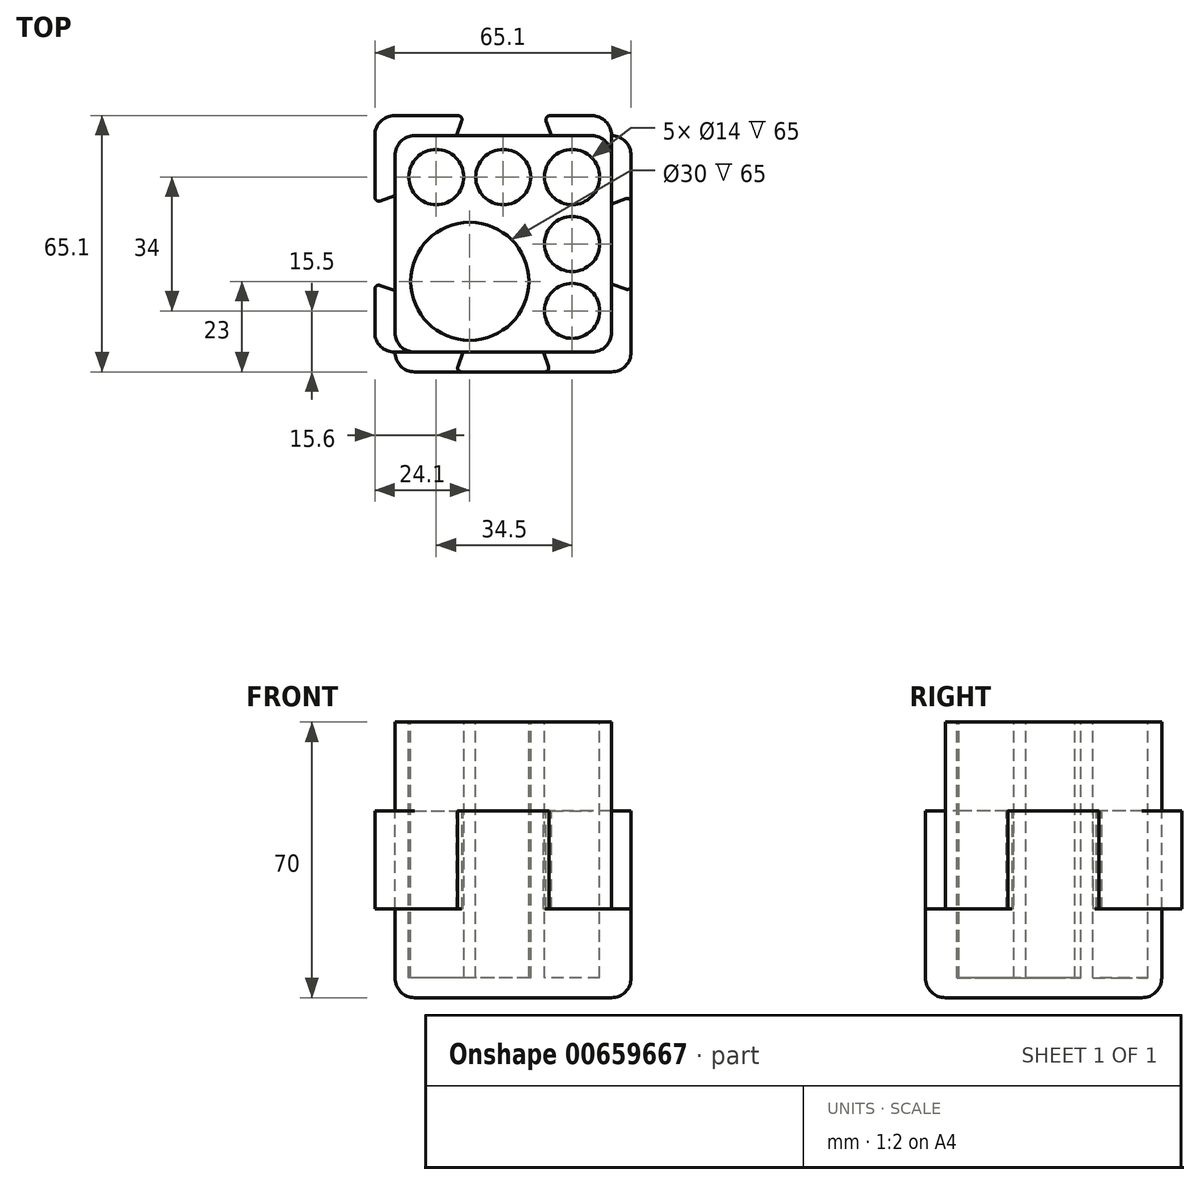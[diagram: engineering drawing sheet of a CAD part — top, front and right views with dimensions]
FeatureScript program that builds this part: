
annotation { "Feature Type Name" : "Feature", "Feature Type Description" : "" }
export const myFeature = defineFeature(function(context is Context, id is Id, definition is map)
    precondition{}
    {
        {
            var Q0;
            Q0=qCreatedBy(makeId("Top.planeOp"),FACE);
            var sketch = newSketch(context, id + "F0", { "sketchPlane" : qUnion([Q0])});
            skLineSegment(sketch, "E0.bottom", {"start": v(-27.5, 27.5) * mm, "end": v(27.5, 27.5) * mm});
            skLineSegment(sketch, "E0.top", {"start": v(-27.5, -27.5) * mm, "end": v(27.5, -27.5) * mm});
            skLineSegment(sketch, "E0.left", {"start": v(-27.5, 27.5) * mm, "end": v(-27.5, -27.5) * mm});
            skLineSegment(sketch, "E0.right", {"start": v(27.5, 27.5) * mm, "end": v(27.5, -27.5) * mm});
            skPoint(sketch, "E0.middle", {"position": v(0, 0) * mm});
            skLineSegment(sketch, "E1", {"start": v(-27.5, 27.5) * mm, "end": v(-32.6, 27.5) * mm});
            skLineSegment(sketch, "E2", {"start": v(-32.6, 27.5) * mm, "end": v(-32.6, 10.44) * mm});
            skLineSegment(sketch, "E3", {"start": v(-32.6, 10.44) * mm, "end": v(-27.5, 12.3) * mm});
            skLineSegment(sketch, "E4", {"start": v(-27.5, -11.9) * mm, "end": v(-32.6, -10.04) * mm});
            skLineSegment(sketch, "E5", {"start": v(-32.6, -10.04) * mm, "end": v(-32.6, -27.5) * mm});
            skLineSegment(sketch, "E6", {"start": v(-32.6, -27.5) * mm, "end": v(-27.5, -27.5) * mm});
            skLineSegment(sketch, "E7", {"start": v(-27.5, 27.5) * mm, "end": v(-27.5, 32.6) * mm});
            skLineSegment(sketch, "E8", {"start": v(-27.5, 32.6) * mm, "end": v(-10.04, 32.6) * mm});
            skLineSegment(sketch, "E9", {"start": v(-10.04, 32.6) * mm, "end": v(-11.9, 27.5) * mm});
            skLineSegment(sketch, "E10", {"start": v(27.5, 27.5) * mm, "end": v(27.5, 32.6) * mm});
            skLineSegment(sketch, "E11", {"start": v(27.5, 32.6) * mm, "end": v(10.44, 32.6) * mm});
            skLineSegment(sketch, "E12", {"start": v(10.44, 32.6) * mm, "end": v(12.3, 27.5) * mm});
            skLineSegment(sketch, "E13", {"start": v(-10.18, -27.5) * mm, "end": v(-12, -32.5) * mm});
            skLineSegment(sketch, "E14", {"start": v(-12, -32.5) * mm, "end": v(12, -32.5) * mm});
            skLineSegment(sketch, "E15", {"start": v(12, -32.5) * mm, "end": v(10.18, -27.5) * mm});
            skPoint(sketch, "E16", {"position": v(0, -32.5) * mm});
            skLineSegment(sketch, "E17", {"start": v(27.5, -10.18) * mm, "end": v(32.5, -12) * mm});
            skLineSegment(sketch, "E18", {"start": v(32.5, -12) * mm, "end": v(32.5, 12) * mm});
            skLineSegment(sketch, "E19", {"start": v(32.5, 12) * mm, "end": v(27.5, 10.18) * mm});
            skPoint(sketch, "E20", {"position": v(32.5, 0) * mm});
            skLineSegment(sketch, "E21", {"start": v(-32.6, 27.5) * mm, "end": v(-32.6, 32.6) * mm});
            skLineSegment(sketch, "E22", {"start": v(-32.6, 32.6) * mm, "end": v(-27.5, 32.6) * mm});
            skSolve(sketch);
        }
        {
            var Q0;
            {var subQ1=sQuery(id+"F0.wireOp",EDGE,"E0.bottom");Q0=makeQuery(id+"F0.imprint","IMPRINT",FACE,{"disambiguationData":[TD([[makeQuery(id+"F0.imprint","IMPRINT",EDGE,{"derivedFrom":subQ1}),-1.0]])]});}
            extrude(context, id + "F1", {"entities" : qUnion([Q0]), "oppositeDirection" : true, "depth" : 70 * mm, "offsetDistance" : 25 * mm, "symmetric" : true});
        }
        {
            var Q0;
            {var subQ0=sQuery(id+"F0.wireOp",EDGE,"E1");Q0=makeQuery(id+"F0.imprint","IMPRINT",FACE,{"disambiguationData":[TD([[makeQuery(id+"F0.imprint","IMPRINT",EDGE,{"derivedFrom":subQ0}),1.0]])]});}
            var Q1;
            {var subQ2=sQuery(id+"F0.wireOp",EDGE,"E4");Q1=makeQuery(id+"F0.imprint","IMPRINT",FACE,{"disambiguationData":[TD([[makeQuery(id+"F0.imprint","IMPRINT",EDGE,{"derivedFrom":subQ2}),1.0]])]});}
            var Q2;
            {var subQ2=sQuery(id+"F0.wireOp",EDGE,"E7");Q2=makeQuery(id+"F0.imprint","IMPRINT",FACE,{"disambiguationData":[TD([[makeQuery(id+"F0.imprint","IMPRINT",EDGE,{"derivedFrom":subQ2}),-1.0]])]});}
            var Q3;
            {var subQ0=sQuery(id+"F0.wireOp",EDGE,"E10");Q3=makeQuery(id+"F0.imprint","IMPRINT",FACE,{"disambiguationData":[TD([[makeQuery(id+"F0.imprint","IMPRINT",EDGE,{"derivedFrom":subQ0}),1.0]])]});}
            var Q4;
            {var subQ2=sQuery(id+"F0.wireOp",EDGE,"E13");Q4=makeQuery(id+"F0.imprint","IMPRINT",FACE,{"disambiguationData":[TD([[makeQuery(id+"F0.imprint","IMPRINT",EDGE,{"derivedFrom":subQ2}),1.0]])]});}
            var Q5;
            {var subQ0=sQuery(id+"F0.wireOp",EDGE,"E17");Q5=makeQuery(id+"F0.imprint","IMPRINT",FACE,{"disambiguationData":[TD([[makeQuery(id+"F0.imprint","IMPRINT",EDGE,{"derivedFrom":subQ0}),1.0]])]});}
            var Q6;
            Q6=makeQuery(id+"F0.imprint","IMPRINT",FACE,{"disambiguationData":[TD([[makeQuery(id+"F0.imprint","IMPRINT",EDGE,{"derivedFrom":sQuery(id+"F0.wireOp",EDGE,"E1")}),-1.0]])]});
            extrude(context, id + "F2", {"entities" : qUnion([Q0, Q1, Q2, Q3, Q4, Q5, Q6]), "operationType" : NewBodyOperationType.ADD, "oppositeDirection" : true, "depth" : 25 * mm, "offsetDistance" : 25 * mm, "symmetric" : true});
        }
        {
            var Q0;
            Q0=makeQuery(id+"F1.opExtrude","CAP_FACE",FACE,{"disambiguationData":[OSD([sQuery(id+"F0.wireOp",EDGE,"E0.bottom"),sQuery(id+"F0.wireOp",EDGE,"E0.top"),sQuery(id+"F0.wireOp",EDGE,"E0.left"),sQuery(id+"F0.wireOp",EDGE,"E0.right")])],"isStart":false});
            var sketch = newSketch(context, id + "F3", { "sketchPlane" : qUnion([Q0])});
            skLineSegment(sketch, "E23", {"start": v(-27.5, 27.5) * mm, "end": v(-27.5, 32.5) * mm});
            skLineSegment(sketch, "E24", {"start": v(-27.5, 32.5) * mm, "end": v(32.5, 32.5) * mm});
            skLineSegment(sketch, "E25", {"start": v(32.5, 32.5) * mm, "end": v(32.5, -27.5) * mm});
            skLineSegment(sketch, "E26", {"start": v(32.5, -27.5) * mm, "end": v(27.5, -27.5) * mm});
            skLineSegment(sketch, "E27", {"start": v(27.5, -27.5) * mm, "end": v(27.5, 27.5) * mm});
            skLineSegment(sketch, "E28", {"start": v(27.5, 27.5) * mm, "end": v(-27.5, 27.5) * mm});
            skSolve(sketch);
        }
        {
            var Q0;
            Q0 = qSketchRegion(id + "F3", true);
            var Q1;
            Q1=makeQuery(id+"F2.opExtrude","CAP_FACE",FACE,{"disambiguationData":[OSD([sQuery(id+"F0.wireOp",EDGE,"E0.right"),sQuery(id+"F0.wireOp",EDGE,"E17"),sQuery(id+"F0.wireOp",EDGE,"E18"),sQuery(id+"F0.wireOp",EDGE,"E19")])],"isStart":false});
            extrude(context, id + "F4", {"entities" : qUnion([Q0]), "operationType" : NewBodyOperationType.ADD, "endBound" : BoundingType.UP_TO_SURFACE, "oppositeDirection" : true, "depth" : 25 * mm, "endBoundEntityFace" : qUnion([Q1]), "offsetDistance" : 25 * mm});
        }
        {
            var Q0;
            Q0=makeQuery(id+"F2.opExtrude","SWEPT_EDGE",EDGE,{"disambiguationData":[OSD([sQuery(id+"F0.wireOp",EDGE,"E21"),sQuery(id+"F0.wireOp",EDGE,"E22")])]});
            var Q1;
            {var subQ0=sQuery(id+"F0.wireOp",EDGE,"E0.bottom");var subQ1=sQuery(id+"F0.wireOp",EDGE,"E0.left");Q1=makeQuery(id+"F2.boolean.opBoolean","SPLIT",EDGE,{"disambiguationData":[TD([makeQuery(id+"F1.opExtrude","CAP_FACE",FACE,{"disambiguationData":[OSD([subQ0,sQuery(id+"F0.wireOp",EDGE,"E0.top"),subQ1,sQuery(id+"F0.wireOp",EDGE,"E0.right")])],"isStart":true})])],"derivedFrom":makeQuery(id+"F1.opExtrude","SWEPT_EDGE",EDGE,{"disambiguationData":[OSD([subQ0,subQ1,sQuery(id+"F0.wireOp",EDGE,"E1"),sQuery(id+"F0.wireOp",EDGE,"E7")])]})});}
            var Q2;
            {var subQ0=sQuery(id+"F0.wireOp",EDGE,"E0.bottom");var subQ1=sQuery(id+"F0.wireOp",EDGE,"E0.left");Q2=makeQuery(id+"F2.boolean.opBoolean","SPLIT",EDGE,{"disambiguationData":[TD([makeQuery(id+"F1.opExtrude","CAP_FACE",FACE,{"disambiguationData":[OSD([subQ0,sQuery(id+"F0.wireOp",EDGE,"E0.top"),subQ1,sQuery(id+"F0.wireOp",EDGE,"E0.right")])],"isStart":false})])],"derivedFrom":makeQuery(id+"F1.opExtrude","SWEPT_EDGE",EDGE,{"disambiguationData":[OSD([subQ0,subQ1,sQuery(id+"F0.wireOp",EDGE,"E1"),sQuery(id+"F0.wireOp",EDGE,"E7")])]})});}
            var Q3;
            Q3=makeQuery(id+"F2.opExtrude","SWEPT_EDGE",EDGE,{"disambiguationData":[OSD([sQuery(id+"F0.wireOp",EDGE,"E5"),sQuery(id+"F0.wireOp",EDGE,"E6")])]});
            var Q4;
            Q4=makeQuery(id+"F4.opExtrude","SWEPT_EDGE",EDGE,{"disambiguationData":[OSD([sQuery(id+"F3.wireOp",EDGE,"E23"),sQuery(id+"F3.wireOp",EDGE,"E24")])]});
            var Q5;
            Q5=makeQuery(id+"F4.opExtrude","SWEPT_EDGE",EDGE,{"disambiguationData":[OSD([sQuery(id+"F3.wireOp",EDGE,"E24"),sQuery(id+"F3.wireOp",EDGE,"E25")])]});
            var Q6;
            Q6=makeQuery(id+"F1.opExtrude","SWEPT_EDGE",EDGE,{"disambiguationData":[OSD([sQuery(id+"F0.wireOp",EDGE,"E0.top"),sQuery(id+"F0.wireOp",EDGE,"E0.right")])]});
            var Q7;
            Q7=makeQuery(id+"F4.opExtrude","SWEPT_EDGE",EDGE,{"disambiguationData":[OSD([sQuery(id+"F3.wireOp",EDGE,"E25"),sQuery(id+"F3.wireOp",EDGE,"E26")])]});
            var Q8;
            Q8=makeQuery(id+"F2.opExtrude","SWEPT_EDGE",EDGE,{"disambiguationData":[OSD([sQuery(id+"F0.wireOp",EDGE,"E10"),sQuery(id+"F0.wireOp",EDGE,"E11")])]});
            var Q9;
            {var subQ0=sQuery(id+"F0.wireOp",EDGE,"E0.right");var subQ1=sQuery(id+"F0.wireOp",EDGE,"E0.bottom");var subQ2=sQuery(id+"F0.wireOp",EDGE,"E10");Q9=makeQuery(id+"F2.boolean.opBoolean","SPLIT",EDGE,{"disambiguationData":[TD([makeQuery(id+"F1.opExtrude","CAP_FACE",FACE,{"disambiguationData":[OSD([subQ1,sQuery(id+"F0.wireOp",EDGE,"E0.top"),sQuery(id+"F0.wireOp",EDGE,"E0.left"),subQ0])],"isStart":true})])],"derivedFrom":makeQuery(id+"F1.opExtrude","SWEPT_EDGE",EDGE,{"disambiguationData":[OSD([subQ1,subQ0,subQ2])]})});}
            var Q10;
            Q10=makeQuery(id+"F4.opExtrude","CAP_EDGE",EDGE,{"disambiguationData":[OSD([sQuery(id+"F3.wireOp",EDGE,"E25")])],"isStart":true});
            var Q11;
            Q11=makeQuery(id+"F4.opExtrude","CAP_EDGE",EDGE,{"disambiguationData":[OSD([sQuery(id+"F3.wireOp",EDGE,"E24")])],"isStart":true});
            var Q12;
            Q12=makeQuery(id+"F4.boolean.opBoolean","MERGE",EDGE,{"derivedFrom":[makeQuery(id+"F1.opExtrude","CAP_EDGE",EDGE,{"disambiguationData":[OSD([sQuery(id+"F0.wireOp",EDGE,"E0.left")])],"isStart":false}),makeQuery(id+"F4.opExtrude","CAP_EDGE",EDGE,{"disambiguationData":[OSD([sQuery(id+"F3.wireOp",EDGE,"E23")])],"isStart":true})]});
            var Q13;
            Q13=makeQuery(id+"F4.boolean.opBoolean","MERGE",EDGE,{"derivedFrom":[makeQuery(id+"F1.opExtrude","CAP_EDGE",EDGE,{"disambiguationData":[OSD([sQuery(id+"F0.wireOp",EDGE,"E0.bottom")])],"isStart":false}),makeQuery(id+"F4.opExtrude","CAP_EDGE",EDGE,{"disambiguationData":[OSD([sQuery(id+"F3.wireOp",EDGE,"E26")])],"isStart":true})]});
            var Q14;
            {var subQ0=sQuery(id+"F0.wireOp",EDGE,"E0.left");var subQ1=sQuery(id+"F0.wireOp",EDGE,"E0.top");var subQ2=sQuery(id+"F0.wireOp",EDGE,"E6");Q14=makeQuery(id+"F2.boolean.opBoolean","SPLIT",EDGE,{"disambiguationData":[TD([makeQuery(id+"F1.opExtrude","CAP_FACE",FACE,{"disambiguationData":[OSD([sQuery(id+"F0.wireOp",EDGE,"E0.bottom"),subQ1,subQ0,sQuery(id+"F0.wireOp",EDGE,"E0.right")])],"isStart":true})])],"derivedFrom":makeQuery(id+"F1.opExtrude","SWEPT_EDGE",EDGE,{"disambiguationData":[OSD([subQ1,subQ0,subQ2])]})});}
            fillet(context, id + "F5", {"entities" : qUnion([Q0, Q1, Q2, Q3, Q4, Q5, Q6, Q7, Q8, Q9, Q10, Q11, Q12, Q13, Q14]), "tangentPropagation" : true, "radius" : 5 * mm, "defaultsChanged" : false, "vertexSettings" : [], "allowEdgeOverflow" : false});
        }
        {
            var Q0;
            Q0=makeQuery(id+"F2.opExtrude","SWEPT_EDGE",EDGE,{"disambiguationData":[OSD([sQuery(id+"F0.wireOp",EDGE,"E14"),sQuery(id+"F0.wireOp",EDGE,"E15")])]});
            var Q1;
            Q1=makeQuery(id+"F2.opExtrude","SWEPT_EDGE",EDGE,{"disambiguationData":[OSD([sQuery(id+"F0.wireOp",EDGE,"E13"),sQuery(id+"F0.wireOp",EDGE,"E14")])]});
            var Q2;
            Q2=makeQuery(id+"F2.opExtrude","SWEPT_EDGE",EDGE,{"disambiguationData":[OSD([sQuery(id+"F0.wireOp",EDGE,"E17"),sQuery(id+"F0.wireOp",EDGE,"E18")])]});
            var Q3;
            Q3=makeQuery(id+"F2.opExtrude","SWEPT_EDGE",EDGE,{"disambiguationData":[OSD([sQuery(id+"F0.wireOp",EDGE,"E18"),sQuery(id+"F0.wireOp",EDGE,"E19")])]});
            var Q4;
            Q4=makeQuery(id+"F2.opExtrude","SWEPT_EDGE",EDGE,{"disambiguationData":[OSD([sQuery(id+"F0.wireOp",EDGE,"E11"),sQuery(id+"F0.wireOp",EDGE,"E12")])]});
            var Q5;
            Q5=makeQuery(id+"F2.opExtrude","SWEPT_EDGE",EDGE,{"disambiguationData":[OSD([sQuery(id+"F0.wireOp",EDGE,"E8"),sQuery(id+"F0.wireOp",EDGE,"E9")])]});
            var Q6;
            Q6=makeQuery(id+"F2.opExtrude","SWEPT_EDGE",EDGE,{"disambiguationData":[OSD([sQuery(id+"F0.wireOp",EDGE,"E2"),sQuery(id+"F0.wireOp",EDGE,"E3")])]});
            var Q7;
            Q7=makeQuery(id+"F2.opExtrude","SWEPT_EDGE",EDGE,{"disambiguationData":[OSD([sQuery(id+"F0.wireOp",EDGE,"E4"),sQuery(id+"F0.wireOp",EDGE,"E5")])]});
            fillet(context, id + "F6", {"entities" : qUnion([Q0, Q1, Q2, Q3, Q4, Q5, Q6, Q7]), "tangentPropagation" : true, "radius" : 1 * mm, "defaultsChanged" : false, "vertexSettings" : [], "allowEdgeOverflow" : false});
        }
        {
            var Q0;
            Q0=makeQuery(id+"F1.opExtrude","CAP_FACE",FACE,{"disambiguationData":[OSD([sQuery(id+"F0.wireOp",EDGE,"E0.bottom"),sQuery(id+"F0.wireOp",EDGE,"E0.top"),sQuery(id+"F0.wireOp",EDGE,"E0.left"),sQuery(id+"F0.wireOp",EDGE,"E0.right")])],"isStart":true});
            var sketch = newSketch(context, id + "F7", { "sketchPlane" : qUnion([Q0])});
            skPoint(sketch, "E29", {"position": v(0, 22.5) * mm});
            skCircle(sketch, "E30", {"center": v(17.5, 0) * mm, "radius": 7 * mm});
            skCircle(sketch, "E31", {"center": v(17.5, 17) * mm, "radius": 7 * mm});
            skCircle(sketch, "E32", {"center": v(17.5, -17) * mm, "radius": 7 * mm});
            skCircle(sketch, "E33", {"center": v(-8.5, -9.5) * mm, "radius": 15 * mm});
            skCircle(sketch, "E34", {"center": v(0, 17) * mm, "radius": 7 * mm});
            skCircle(sketch, "E35", {"center": v(-17, 17) * mm, "radius": 7 * mm});
            skSolve(sketch);
        }
        {
            var Q0;
            Q0=makeQuery(id+"F7.imprint","IMPRINT",FACE,{"disambiguationData":[TD([[makeQuery(id+"F7.imprint","IMPRINT",EDGE,{"derivedFrom":sQuery(id+"F7.wireOp",EDGE,"E31")}),1.0]])]});
            var Q1;
            Q1=makeQuery(id+"F7.imprint","IMPRINT",FACE,{"disambiguationData":[TD([[makeQuery(id+"F7.imprint","IMPRINT",EDGE,{"derivedFrom":sQuery(id+"F7.wireOp",EDGE,"E30")}),1.0]])]});
            var Q2;
            Q2=makeQuery(id+"F7.imprint","IMPRINT",FACE,{"disambiguationData":[TD([[makeQuery(id+"F7.imprint","IMPRINT",EDGE,{"derivedFrom":sQuery(id+"F7.wireOp",EDGE,"E32")}),1.0]])]});
            var Q3;
            Q3=makeQuery(id+"F7.imprint","IMPRINT",FACE,{"disambiguationData":[TD([[makeQuery(id+"F7.imprint","IMPRINT",EDGE,{"derivedFrom":sQuery(id+"F7.wireOp",EDGE,"E35")}),1.0]])]});
            var Q4;
            Q4=makeQuery(id+"F7.imprint","IMPRINT",FACE,{"disambiguationData":[TD([[makeQuery(id+"F7.imprint","IMPRINT",EDGE,{"derivedFrom":sQuery(id+"F7.wireOp",EDGE,"E34")}),1.0]])]});
            var Q5;
            Q5=makeQuery(id+"F7.imprint","IMPRINT",FACE,{"disambiguationData":[TD([[makeQuery(id+"F7.imprint","IMPRINT",EDGE,{"derivedFrom":sQuery(id+"F7.wireOp",EDGE,"E33")}),1.0]])]});
            extrude(context, id + "F8", {"entities" : qUnion([Q0, Q1, Q2, Q3, Q4, Q5]), "operationType" : NewBodyOperationType.REMOVE, "oppositeDirection" : true, "depth" : 65 * mm, "offsetDistance" : 25 * mm});
        }
    });
